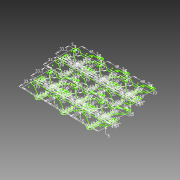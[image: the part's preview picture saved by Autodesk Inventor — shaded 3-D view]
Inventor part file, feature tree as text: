
AUTODESK INVENTOR PART (.ipt)
format: ipt  version: 2012 (Build 160160000, 160)  size: 479,744 bytes
history: native  units: mm
features: sketch x1
ambient origin geometry x8: Origin, YZ Plane, XZ Plane, XY Plane, X Axis, Y Axis, Z Axis, Center Point
feature tree (1):
  sketch  "Sketch1"  dims[d0=1.25mm d1=2.5mm d2=19.8mm d3=5.0mm d4=9.4mm d5=2.5mm d6=1.0mm d7=1.0mm d8=1.0mm d9=5.0mm d10=10.0mm d11=10.0mm d12=2.0mm d13=10.0mm d14=10.0mm d15=4.5mm d16=4.5mm d17=4.5mm d18=4.5mm d19=4.0mm d20=48.0mm d21=48.0mm d22=40.0mm d23=40.0mm d24=10.0mm d25=10.0mm d26=4.0mm d27=4.0mm d28=4.0mm d29=6.75mm d30=60.0mm d31=33.2mm d32=1.25mm d33=2.5mm d34=19.8mm d35=5.0mm d36=9.4mm d37=2.5mm d38=1.0mm d39=5.0mm d40=5.0mm d41=10.0mm d42=10.0mm d43=5.0mm d44=3.0mm d45=3.0mm d46=48.0mm d47=10.0mm d48=60.0mm d49=6.75mm d50=0.75mm d51=5.25mm d52=5.0mm d53=33.2mm d54=1.25mm d55=2.5mm d56=19.8mm d57=5.0mm d58=9.4mm d59=2.5mm d60=1.0mm d61=1.0mm d62=1.0mm d63=5.0mm d64=10.0mm d65=10.0mm d66=2.0mm d67=10.0mm d68=10.0mm d69=4.5mm d70=4.5mm d71=4.5mm d72=4.5mm d73=4.0mm d74=48.0mm d75=48.0mm d76=40.0mm d77=40.0mm d78=10.0mm d79=10.0mm d80=4.0mm d81=4.0mm d82=4.0mm d83=6.75mm d84=60.0mm d85=33.2mm d86=1.25mm d87=2.5mm d88=19.8mm d89=5.0mm d90=9.4mm d91=2.5mm d92=1.0mm d93=5.0mm d94=5.0mm d95=10.0mm d96=10.0mm d97=5.0mm d98=3.0mm d99=3.0mm d100=48.0mm d101=10.0mm d102=60.0mm d103=6.75mm d104=0.75mm d105=5.25mm d106=5.0mm d107=33.2mm d108=1.25mm d109=2.5mm d110=19.8mm d111=5.0mm d112=9.4mm d113=2.5mm d114=1.0mm d115=1.0mm d116=1.0mm d117=5.0mm d118=10.0mm d119=10.0mm d120=2.0mm d121=10.0mm d122=10.0mm d123=4.5mm d124=4.5mm d125=4.5mm d126=4.5mm d127=4.0mm d128=48.0mm d129=48.0mm d130=40.0mm d131=40.0mm d132=10.0mm d133=10.0mm d134=4.0mm d135=4.0mm d136=4.0mm d137=6.75mm d138=60.0mm d139=33.2mm d140=1.25mm d141=2.5mm d142=19.8mm d143=5.0mm d144=9.4mm d145=2.5mm d146=1.0mm d147=5.0mm d148=5.0mm d149=10.0mm d150=10.0mm d151=5.0mm d152=3.0mm d153=3.0mm d154=48.0mm d155=10.0mm d156=60.0mm d157=6.75mm d158=0.75mm d159=5.25mm d160=5.0mm d161=33.2mm d162=1.25mm d163=2.5mm d164=19.8mm d165=5.0mm d166=9.4mm d167=2.5mm d168=1.0mm d169=1.0mm d170=1.0mm d171=5.0mm d172=10.0mm d173=10.0mm d174=2.0mm d175=10.0mm d176=10.0mm d177=4.5mm d178=4.5mm d179=4.5mm d180=4.5mm d181=4.0mm d182=48.0mm d183=48.0mm d184=40.0mm d185=40.0mm d186=10.0mm d187=10.0mm d188=4.0mm d189=4.0mm d190=4.0mm d191=6.75mm d192=60.0mm d193=33.2mm d194=1.25mm d195=2.5mm d196=19.8mm d197=5.0mm d198=9.4mm d199=2.5mm d200=1.0mm d201=5.0mm d202=5.0mm d203=10.0mm d204=10.0mm d205=5.0mm d206=3.0mm d207=3.0mm d208=48.0mm d209=10.0mm d210=60.0mm d211=6.75mm d212=0.75mm d213=5.25mm d214=5.0mm d215=33.2mm d216=1.25mm d217=2.5mm d218=19.8mm d219=5.0mm d220=9.4mm d221=2.5mm d222=1.0mm d223=1.0mm d224=1.0mm d225=5.0mm d226=10.0mm d227=10.0mm d228=2.0mm d229=10.0mm d230=10.0mm d231=4.5mm d232=4.5mm d233=4.5mm d234=4.5mm d235=4.0mm d236=48.0mm d237=48.0mm d238=40.0mm d239=40.0mm d240=10.0mm d241=10.0mm d242=4.0mm d243=4.0mm d244=4.0mm d245=6.75mm d246=60.0mm d247=33.2mm d248=1.25mm d249=2.5mm d250=19.8mm d251=5.0mm d252=9.4mm d253=2.5mm d254=1.0mm d255=5.0mm d256=5.0mm d257=10.0mm d258=10.0mm d259=5.0mm d260=3.0mm d261=3.0mm d262=48.0mm d263=10.0mm d264=60.0mm d265=6.75mm d266=0.75mm d267=5.25mm d268=5.0mm d269=33.2mm d270=1.25mm d271=2.5mm d272=19.8mm d273=5.0mm d274=9.4mm d275=2.5mm d276=1.0mm d277=1.0mm d278=1.0mm d279=5.0mm d280=10.0mm d281=10.0mm d282=2.0mm d283=10.0mm d284=10.0mm d285=4.5mm d286=4.5mm d287=4.5mm d288=4.5mm d289=4.0mm d290=48.0mm d291=48.0mm d292=40.0mm d293=40.0mm d294=10.0mm d295=10.0mm d296=4.0mm d297=4.0mm d298=4.0mm d299=6.75mm d300=60.0mm d301=33.2mm d302=1.25mm d303=2.5mm d304=19.8mm d305=5.0mm d306=9.4mm d307=2.5mm d308=1.0mm d309=5.0mm d310=5.0mm d311=10.0mm d312=10.0mm d313=5.0mm d314=3.0mm d315=3.0mm d316=48.0mm d317=10.0mm d318=60.0mm d319=6.75mm d320=0.75mm d321=5.25mm d322=5.0mm d323=33.2mm]
